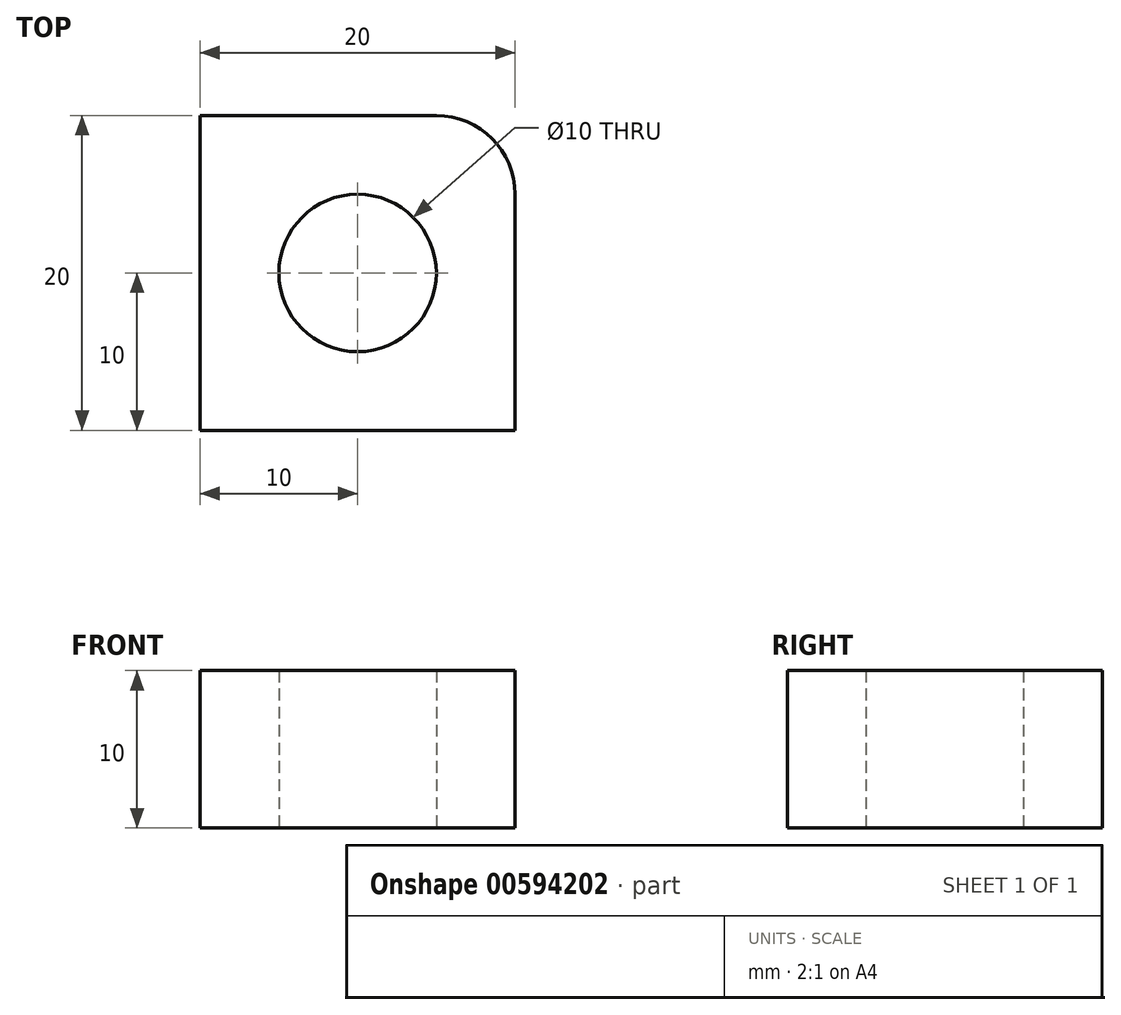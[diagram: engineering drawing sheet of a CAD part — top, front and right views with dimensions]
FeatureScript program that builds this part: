
annotation { "Feature Type Name" : "Feature", "Feature Type Description" : "" }
export const myFeature = defineFeature(function(context is Context, id is Id, definition is map)
    precondition{}
    {
        {
            var Q0;
            Q0=qCreatedBy(makeId("Top.planeOp"),FACE);
            var sketch = newSketch(context, id + "F0", { "sketchPlane" : qUnion([Q0])});
            skLineSegment(sketch, "E0.bottom", {"start": v(-10, 10) * mm, "end": v(5, 10) * mm});
            skLineSegment(sketch, "E0.top", {"start": v(-10, -10) * mm, "end": v(10, -10) * mm});
            skLineSegment(sketch, "E0.left", {"start": v(-10, 10) * mm, "end": v(-10, -10) * mm});
            skLineSegment(sketch, "E0.right", {"start": v(10, 5) * mm, "end": v(10, -10) * mm});
            skPoint(sketch, "E0.middle", {"position": v(0, 0) * mm});
            skCircle(sketch, "E1", {"center": v(0, 0) * mm, "radius": 5 * mm});
            skPoint(sketch, "E2.visualSharp", {"position": v(10, 10) * mm});
            skArc(sketch, "E2.filletArc", {"start": v(10, 5) * mm, "mid": v(8.54, 8.54) * mm, "end": v(5, 10) * mm});
            skSolve(sketch);
        }
        {
            var Q0;
            Q0=makeQuery(id+"F0.imprint","IMPRINT",FACE,{"disambiguationData":[TD([[makeQuery(id+"F0.imprint","IMPRINT",EDGE,{"derivedFrom":sQuery(id+"F0.wireOp",EDGE,"E0.bottom")}),-1.0]])]});
            extrude(context, id + "F1", {"entities" : qUnion([Q0]), "depth" : 10 * mm, "offsetDistance" : 25 * mm});
        }
    });
